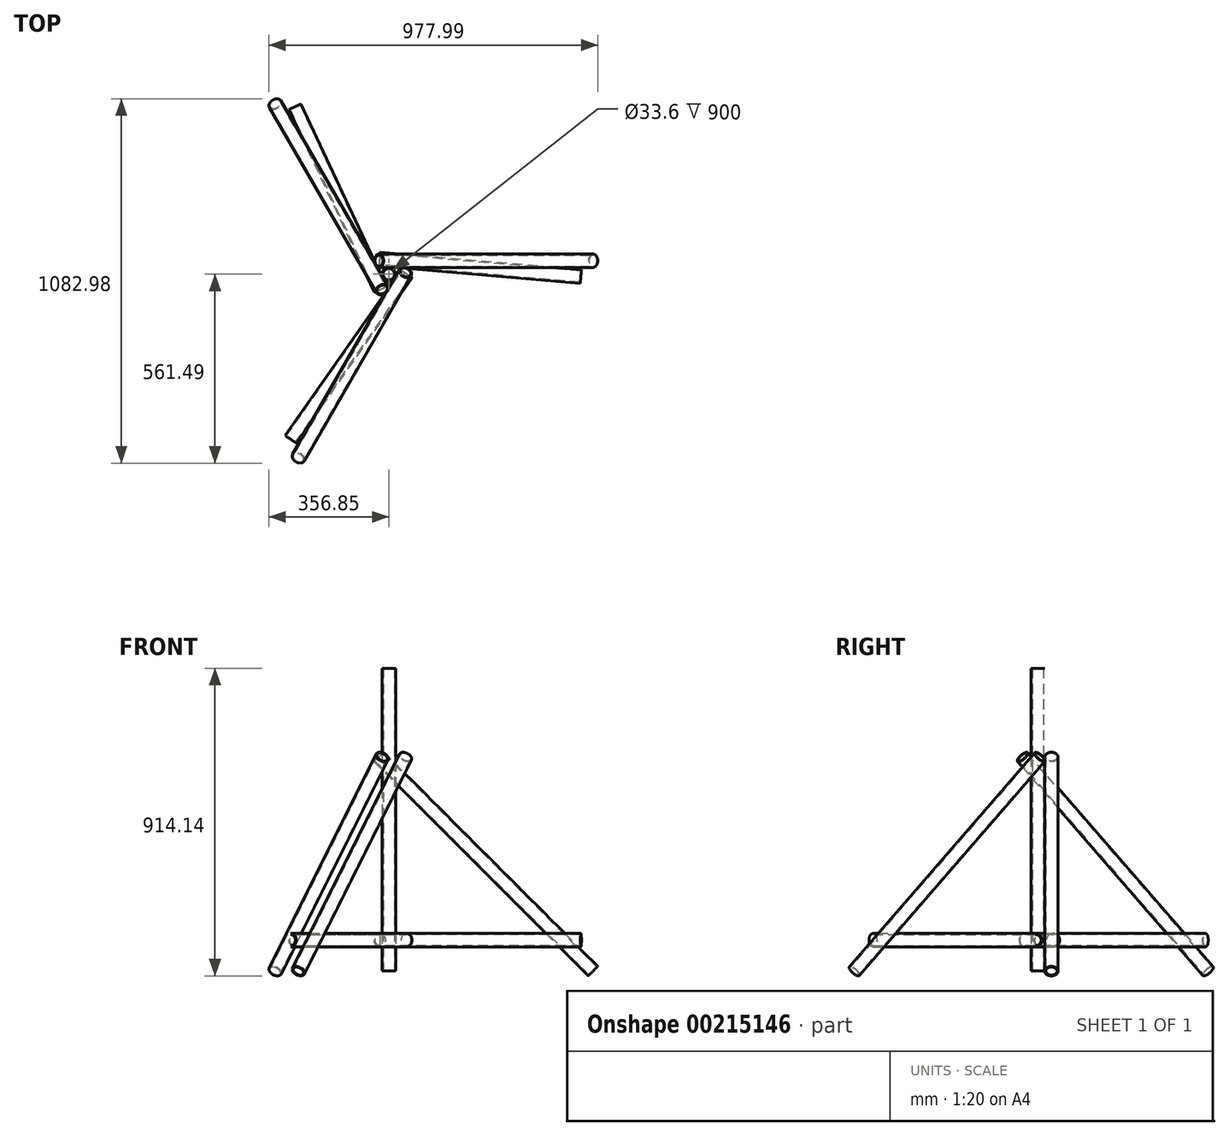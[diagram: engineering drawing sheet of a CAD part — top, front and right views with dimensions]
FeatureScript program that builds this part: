
annotation { "Feature Type Name" : "Feature", "Feature Type Description" : "" }
export const myFeature = defineFeature(function(context is Context, id is Id, definition is map)
    precondition{}
    {
        {
            var Q0;
            Q0=qCreatedBy(makeId("Top.planeOp"),FACE);
            var sketch = newSketch(context, id + "F0", { "sketchPlane" : qUnion([Q0])});
            skCircle(sketch, "E0", {"center": v(0, 0) * mm, "radius": 20 * mm});
            skCircle(sketch, "E1", {"center": v(0, 0) * mm, "radius": 16.8 * mm});
            skLineSegment(sketch, "E2", {"start": v(0, -160.3) * mm, "end": v(0, 187.11) * mm, "construction": true});
            skSolve(sketch);
        }
        {
            var Q0;
            Q0 = qSketchRegion(id + "F0", true);
            extrude(context, id + "F1", {"entities" : qUnion([Q0]), "depth" : 900 * mm, "offsetDistance" : 25 * mm});
        }
        {
            var Q0;
            Q0 = qSketchRegion(id + "F0", true);
            extrude(context, id + "F2", {"entities" : qUnion([Q0]), "depth" : 600 * mm, "offsetDistance" : 25 * mm});
        }
        {
            var Q0;
            Q0=makeQuery(id+"F2.opExtrude","SWEPT_BODY",BODY,{"disambiguationData":[OSD([sQuery(id+"F0.wireOp",EDGE,"E0"),sQuery(id+"F0.wireOp",EDGE,"E1")])]});
            var Q1;
            Q1=sQuery(id+"F0.wireOp",EDGE,"E2");
            transform(context, id + "F3", {"entities" : qUnion([Q0]), "transformType" : TransformType.ROTATION, "transformAxis" : qUnion([Q1]), "angle" : 90 * degree, "makeCopy" : false});
        }
        {
            var Q0;
            Q0=makeQuery(id+"F2.opExtrude","SWEPT_BODY",BODY,{"disambiguationData":[OSD([sQuery(id+"F0.wireOp",EDGE,"E0"),sQuery(id+"F0.wireOp",EDGE,"E1")])]});
            var Q1;
            Q1=makeQuery(id+"F1.opExtrude","SWEPT_FACE",FACE,{"disambiguationData":[OSD([sQuery(id+"F0.wireOp",EDGE,"E0")])]});
            transform(context, id + "F4", {"entities" : qUnion([Q0]), "transformType" : TransformType.ROTATION, "transformAxis" : qUnion([Q1]), "angle" : 5 * degree, "makeCopy" : false});
        }
        {
            var Q0;
            Q0=makeQuery(id+"F2.opExtrude","SWEPT_BODY",BODY,{"disambiguationData":[OSD([sQuery(id+"F0.wireOp",EDGE,"E0"),sQuery(id+"F0.wireOp",EDGE,"E1")])]});
            transform(context, id + "F5", {"entities" : qUnion([Q0]), "transformType" : TransformType.TRANSLATION_3D, "dx" : -27 * mm, "dy" : 45 * mm, "dz" : 92 * mm, "makeCopy" : false});
        }
        {
            var Q0;
            Q0=makeQuery(id+"F1.opExtrude","SWEPT_BODY",BODY,{"disambiguationData":[OSD([sQuery(id+"F0.wireOp",EDGE,"E0"),sQuery(id+"F0.wireOp",EDGE,"E1")])]});
            var Q1;
            Q1=sQuery(id+"F0.wireOp",EDGE,"E2");
            transform(context, id + "F6", {"entities" : qUnion([Q0]), "transformType" : TransformType.ROTATION, "transformAxis" : qUnion([Q1]), "angle" : 45 * degree, "oppositeDirection" : true, "makeCopy" : true});
        }
        {
            var Q0;
            Q0=makeQuery(id+"F6.opPattern","COPY",BODY,{"derivedFrom":makeQuery(id+"F1.opExtrude","SWEPT_BODY",BODY,{"disambiguationData":[OSD([sQuery(id+"F0.wireOp",EDGE,"E0"),sQuery(id+"F0.wireOp",EDGE,"E1")])]}),"instanceName":"1"});
            transform(context, id + "F7", {"entities" : qUnion([Q0]), "transformType" : TransformType.TRANSLATION_3D, "dx" : 607 * mm, "dy" : 40 * mm, "dz" : 0 * mm, "makeCopy" : false});
        }
        {
            var Q0;
            Q0=makeQuery(id+"F6.opPattern","COPY",BODY,{"derivedFrom":makeQuery(id+"F1.opExtrude","SWEPT_BODY",BODY,{"disambiguationData":[OSD([sQuery(id+"F0.wireOp",EDGE,"E0"),sQuery(id+"F0.wireOp",EDGE,"E1")])]}),"instanceName":"1"});
            var Q1;
            Q1=makeQuery(id+"F2.opExtrude","SWEPT_BODY",BODY,{"disambiguationData":[OSD([sQuery(id+"F0.wireOp",EDGE,"E0"),sQuery(id+"F0.wireOp",EDGE,"E1")])]});
            var Q2;
            Q2=makeQuery(id+"F1.opExtrude","SWEPT_FACE",FACE,{"disambiguationData":[OSD([sQuery(id+"F0.wireOp",EDGE,"E0")])]});
            transform(context, id + "F8", {"entities" : qUnion([Q0, Q1]), "transformType" : TransformType.ROTATION, "transformAxis" : qUnion([Q2]), "angle" : 120 * degree, "makeCopy" : true});
        }
        {
            var Q0;
            Q0=makeQuery(id+"F8.opPattern","COPY",BODY,{"derivedFrom":makeQuery(id+"F6.opPattern","COPY",BODY,{"derivedFrom":makeQuery(id+"F1.opExtrude","SWEPT_BODY",BODY,{"disambiguationData":[OSD([sQuery(id+"F0.wireOp",EDGE,"E0"),sQuery(id+"F0.wireOp",EDGE,"E1")])]}),"instanceName":"1"}),"instanceName":"1"});
            var Q1;
            Q1=makeQuery(id+"F8.opPattern","COPY",BODY,{"derivedFrom":makeQuery(id+"F2.opExtrude","SWEPT_BODY",BODY,{"disambiguationData":[OSD([sQuery(id+"F0.wireOp",EDGE,"E0"),sQuery(id+"F0.wireOp",EDGE,"E1")])]}),"instanceName":"1"});
            var Q2;
            Q2=makeQuery(id+"F1.opExtrude","SWEPT_FACE",FACE,{"disambiguationData":[OSD([sQuery(id+"F0.wireOp",EDGE,"E0")])]});
            transform(context, id + "F9", {"entities" : qUnion([Q0, Q1]), "transformType" : TransformType.ROTATION, "transformAxis" : qUnion([Q2]), "angle" : 120 * degree, "makeCopy" : true});
        }
    });
